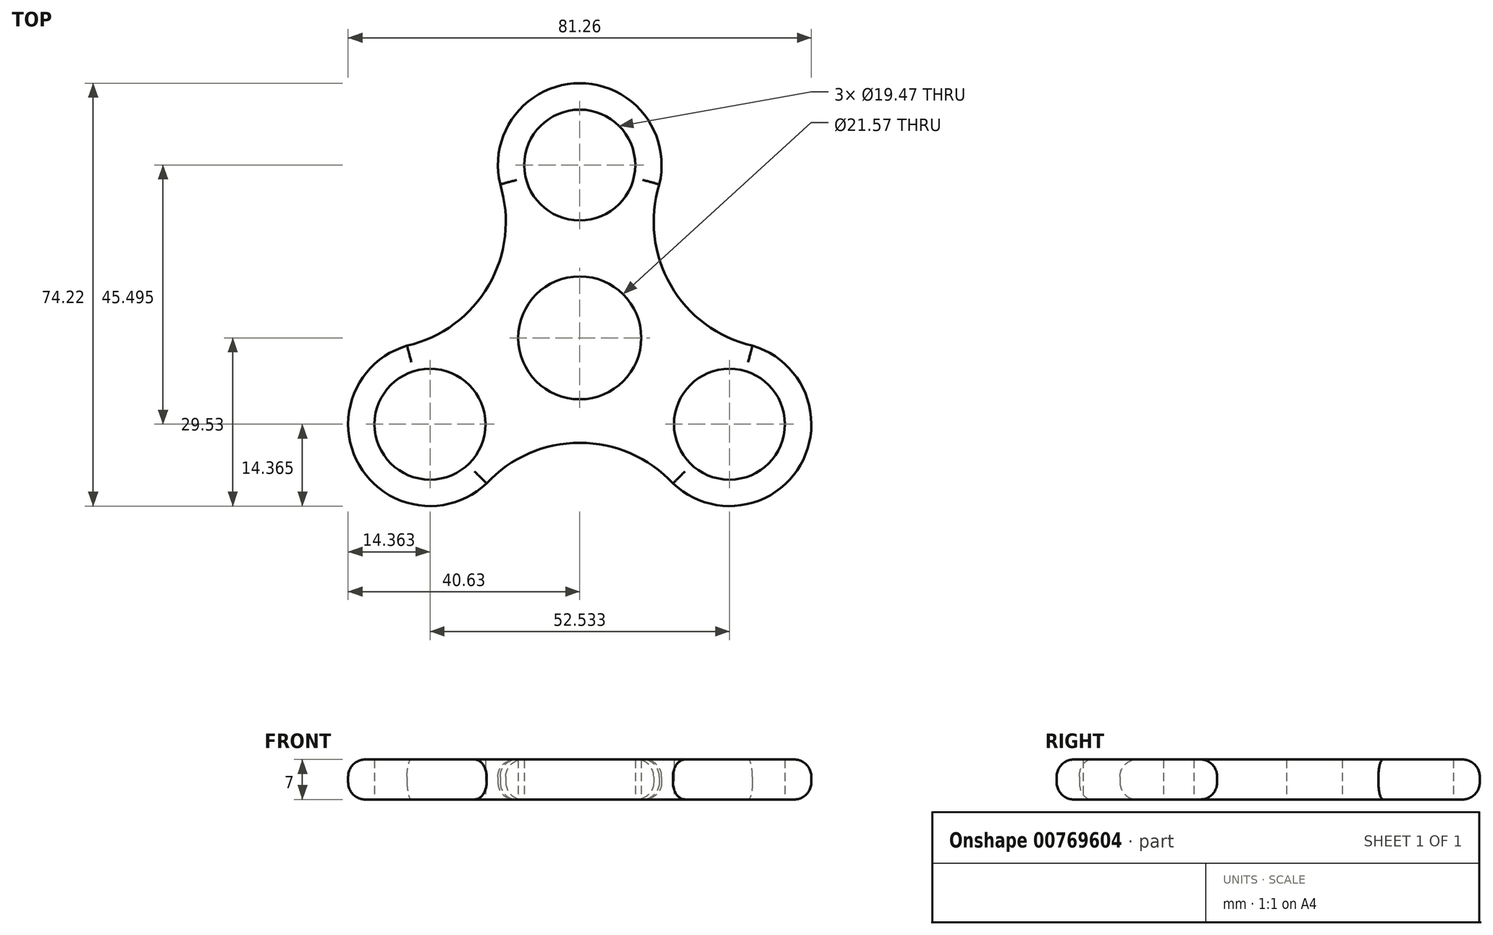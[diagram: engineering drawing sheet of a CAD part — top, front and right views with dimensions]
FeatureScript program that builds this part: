
annotation { "Feature Type Name" : "Feature", "Feature Type Description" : "" }
export const myFeature = defineFeature(function(context is Context, id is Id, definition is map)
    precondition{}
    {
        {
            var Q0;
            Q0=qCreatedBy(makeId("Top.planeOp"),FACE);
            var sketch = newSketch(context, id + "F0", { "sketchPlane" : qUnion([Q0])});
            skCircle(sketch, "E0", {"center": v(0, 30.33) * mm, "radius": 14.36 * mm});
            skCircle(sketch, "E1.1.0", {"center": v(-26.27, -15.17) * mm, "radius": 14.36 * mm});
            skCircle(sketch, "E1.2.0", {"center": v(26.27, -15.17) * mm, "radius": 14.36 * mm});
            skPoint(sketch, "E1.center", {"position": v(0, 0) * mm});
            skArc(sketch, "E2", {"start": v(-30.3, -1.38) * mm, "mid": v(-15.96, 9.21) * mm, "end": v(-13.95, 26.93) * mm});
            skArc(sketch, "E3.1.0", {"start": v(16.34, -25.55) * mm, "mid": v(0, -18.43) * mm, "end": v(-16.34, -25.55) * mm});
            skArc(sketch, "E3.2.0", {"start": v(13.95, 26.93) * mm, "mid": v(15.96, 9.21) * mm, "end": v(30.3, -1.38) * mm});
            skCircle(sketch, "E4", {"center": v(0, 30.33) * mm, "radius": 9.73 * mm});
            skCircle(sketch, "E5", {"center": v(0, 0) * mm, "radius": 10.79 * mm});
            skCircle(sketch, "E6.1.0", {"center": v(-26.27, -15.17) * mm, "radius": 9.73 * mm});
            skCircle(sketch, "E6.2.0", {"center": v(26.27, -15.17) * mm, "radius": 9.73 * mm});
            skSolve(sketch);
        }
        {
            var Q0;
            Q0=makeQuery(id+"F0.imprint","IMPRINT",FACE,{"disambiguationData":[TD([[makeQuery(id+"F0.imprint","IMPRINT",EDGE,{"derivedFrom":sQuery(id+"F0.wireOp",EDGE,"E5")}),-1.0]])]});
            var Q1;
            Q1=makeQuery(id+"F0.imprint","IMPRINT",FACE,{"disambiguationData":[TD([[makeQuery(id+"F0.imprint","IMPRINT",EDGE,{"derivedFrom":sQuery(id+"F0.wireOp",EDGE,"E4")}),-1.0]])]});
            var Q2;
            Q2=makeQuery(id+"F0.imprint","IMPRINT",FACE,{"disambiguationData":[TD([[makeQuery(id+"F0.imprint","IMPRINT",EDGE,{"derivedFrom":sQuery(id+"F0.wireOp",EDGE,"E6.2.0")}),-1.0]])]});
            var Q3;
            Q3=makeQuery(id+"F0.imprint","IMPRINT",FACE,{"disambiguationData":[TD([[makeQuery(id+"F0.imprint","IMPRINT",EDGE,{"derivedFrom":sQuery(id+"F0.wireOp",EDGE,"E6.1.0")}),-1.0]])]});
            extrude(context, id + "F1", {"entities" : qUnion([Q0, Q1, Q2, Q3]), "depth" : 7 * mm, "offsetDistance" : 25 * mm});
        }
        {
            var Q0;
            Q0=makeQuery(id+"F1.opExtrude","CAP_EDGE",EDGE,{"disambiguationData":[OSD([sQuery(id+"F0.wireOp",EDGE,"E2")])],"isStart":false});
            var Q1;
            Q1=makeQuery(id+"F1.opExtrude","CAP_EDGE",EDGE,{"disambiguationData":[OSD([sQuery(id+"F0.wireOp",EDGE,"E0")])],"isStart":false});
            var Q2;
            Q2=makeQuery(id+"F1.opExtrude","CAP_EDGE",EDGE,{"disambiguationData":[OSD([sQuery(id+"F0.wireOp",EDGE,"E3.2.0")])],"isStart":false});
            var Q3;
            Q3=makeQuery(id+"F1.opExtrude","CAP_EDGE",EDGE,{"disambiguationData":[OSD([sQuery(id+"F0.wireOp",EDGE,"E1.2.0")])],"isStart":false});
            var Q4;
            Q4=makeQuery(id+"F1.opExtrude","CAP_EDGE",EDGE,{"disambiguationData":[OSD([sQuery(id+"F0.wireOp",EDGE,"E3.1.0")])],"isStart":false});
            var Q5;
            Q5=makeQuery(id+"F1.opExtrude","CAP_EDGE",EDGE,{"disambiguationData":[OSD([sQuery(id+"F0.wireOp",EDGE,"E1.1.0")])],"isStart":false});
            var Q6;
            Q6=makeQuery(id+"F1.opExtrude","CAP_EDGE",EDGE,{"disambiguationData":[OSD([sQuery(id+"F0.wireOp",EDGE,"E3.1.0")])],"isStart":true});
            var Q7;
            Q7=makeQuery(id+"F1.opExtrude","CAP_EDGE",EDGE,{"disambiguationData":[OSD([sQuery(id+"F0.wireOp",EDGE,"E1.1.0")])],"isStart":true});
            var Q8;
            Q8=makeQuery(id+"F1.opExtrude","CAP_EDGE",EDGE,{"disambiguationData":[OSD([sQuery(id+"F0.wireOp",EDGE,"E2")])],"isStart":true});
            var Q9;
            Q9=makeQuery(id+"F1.opExtrude","CAP_EDGE",EDGE,{"disambiguationData":[OSD([sQuery(id+"F0.wireOp",EDGE,"E0")])],"isStart":true});
            var Q10;
            Q10=makeQuery(id+"F1.opExtrude","CAP_EDGE",EDGE,{"disambiguationData":[OSD([sQuery(id+"F0.wireOp",EDGE,"E3.2.0")])],"isStart":true});
            var Q11;
            Q11=makeQuery(id+"F1.opExtrude","CAP_EDGE",EDGE,{"disambiguationData":[OSD([sQuery(id+"F0.wireOp",EDGE,"E1.2.0")])],"isStart":true});
            fillet(context, id + "F2", {"entities" : qUnion([Q0, Q1, Q2, Q3, Q4, Q5, Q6, Q7, Q8, Q9, Q10, Q11]), "radius" : 3 * mm, "tangentPropagation" : true, "allowEdgeOverflow" : false});
        }
    });
